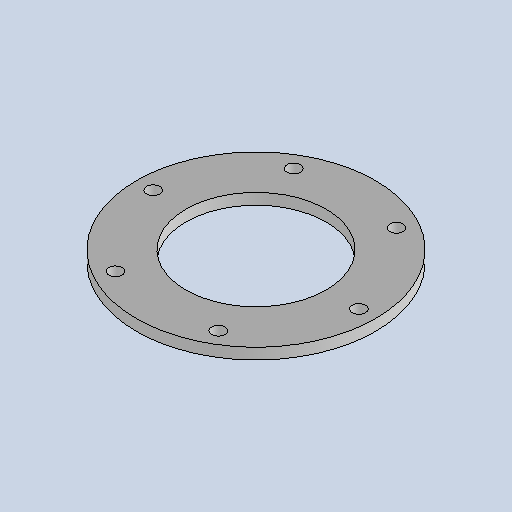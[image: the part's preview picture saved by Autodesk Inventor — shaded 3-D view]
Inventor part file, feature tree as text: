
AUTODESK INVENTOR PART (.ipt)
format: ipt  version: 2025 (Build 290162010, 162A)  size: 297,984 bytes
history: native  units: mm
features: sketch x2, other x2, extrude x1, pattern_circular x1
ambient origin geometry x8: Origin, YZ Plane, XZ Plane, XY Plane, X Axis, Y Axis, Z Axis, Center Point
bodies: Solid1 (feature_tree)
feature tree (6):
  extrude  "Extrusion1"  Depth=215.0mm
  pattern_circular  "Circular Pattern1"  [2 undecoded]
  sketch  "Sketch1"  dims[d0=126.0mm d1=215.0mm]
  sketch  "Sketch3"  dims[d2=10.0mm d3=0.0mm d4=185.0mm d5=12.0mm d6=10.0mm d7=10.0mm d8=0.0mm d9=60.0mm d10=360.0deg]
  other  "Cut1"
  other  "Definition1"
note: 2 required parameter values undecoded (feature->parameter linkage not recoverable at this tier; creation-order binding heuristic only, values carry confidence <= 0.55)
